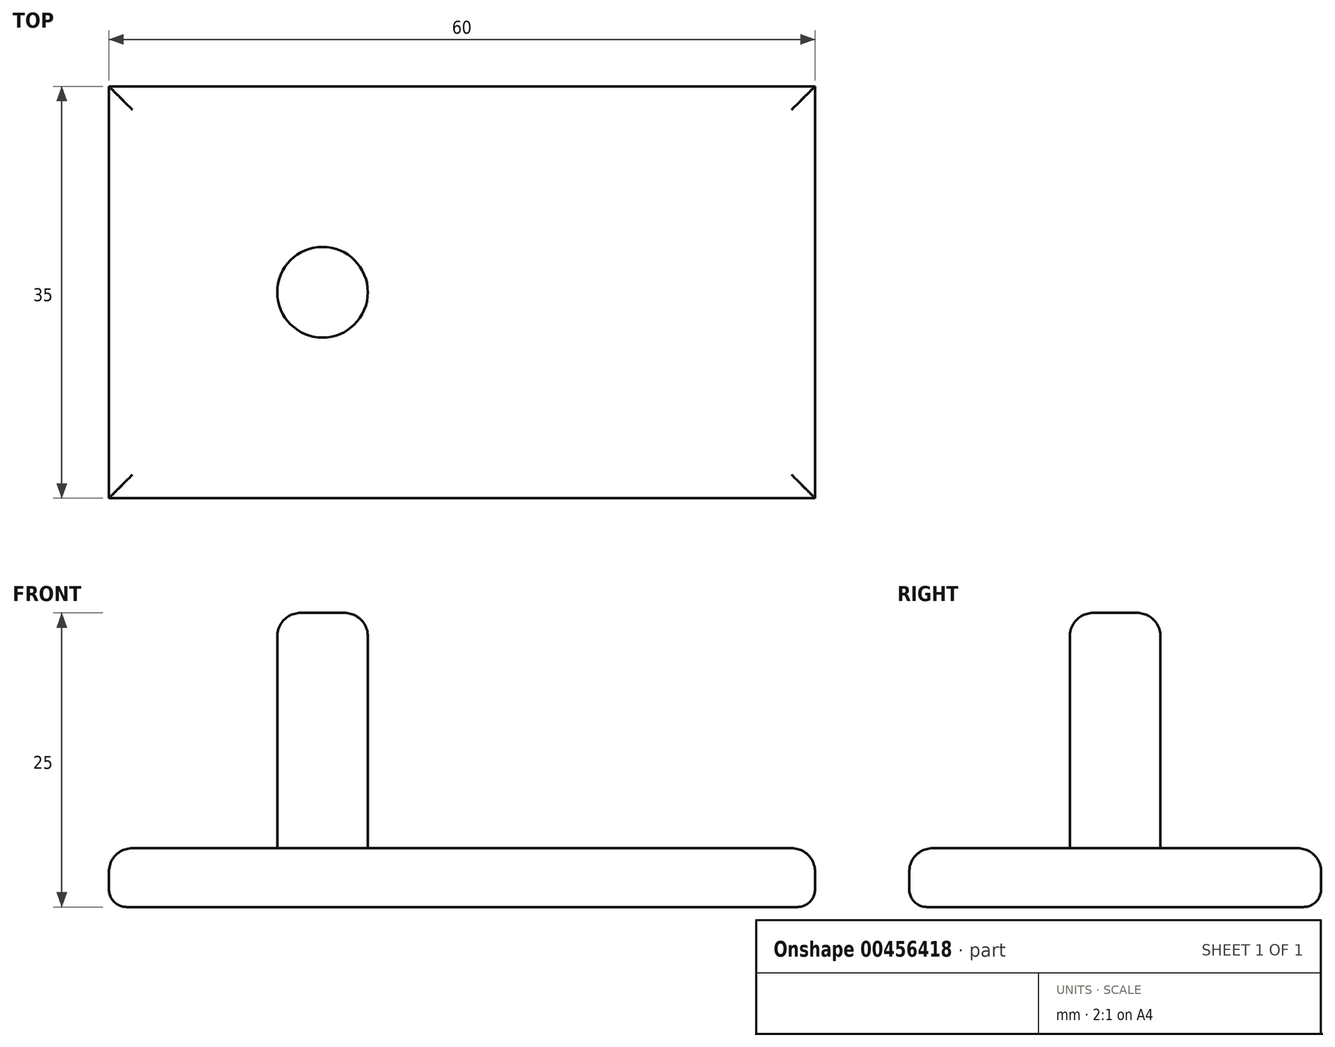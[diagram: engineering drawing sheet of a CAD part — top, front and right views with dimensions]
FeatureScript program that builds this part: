
annotation { "Feature Type Name" : "Feature", "Feature Type Description" : "" }
export const myFeature = defineFeature(function(context is Context, id is Id, definition is map)
    precondition{}
    {
        {
            var Q0;
            Q0=qCreatedBy(makeId("Top.planeOp"),FACE);
            var sketch = newSketch(context, id + "F0", { "sketchPlane" : qUnion([Q0])});
            skLineSegment(sketch, "E0.bottom", {"start": v(-30, 17.5) * mm, "end": v(30, 17.5) * mm});
            skLineSegment(sketch, "E0.top", {"start": v(-30, -17.5) * mm, "end": v(30, -17.5) * mm});
            skLineSegment(sketch, "E0.left", {"start": v(-30, 17.5) * mm, "end": v(-30, -17.5) * mm});
            skLineSegment(sketch, "E0.right", {"start": v(30, 17.5) * mm, "end": v(30, -17.5) * mm});
            skPoint(sketch, "E0.middle", {"position": v(0, 0) * mm});
            skPoint(sketch, "E1.orphan", {"position": v(0, 37.9) * mm});
            skPoint(sketch, "E2.orphan", {"position": v(-61.07, 0) * mm});
            skSolve(sketch);
        }
        {
            var Q0;
            Q0 = qSketchRegion(id + "F0", true);
            extrude(context, id + "F1", {"entities" : qUnion([Q0]), "oppositeDirection" : true, "depth" : 5 * mm});
        }
        {
            var Q0;
            Q0=qCreatedBy(makeId("Top.planeOp"),FACE);
            var sketch = newSketch(context, id + "F2", { "sketchPlane" : qUnion([Q0])});
            skLineSegment(sketch, "E3", {"start": v(-47.54, 0) * mm, "end": v(45.98, 0) * mm, "construction": true});
            skLineSegment(sketch, "E4", {"start": v(45.98, 0) * mm, "end": v(46.2, 1.35) * mm, "construction": true});
            skLineSegment(sketch, "E5", {"start": v(0, 46.27) * mm, "end": v(0, -44.87) * mm, "construction": true});
            skCircle(sketch, "E6", {"center": v(-11.85, 0) * mm, "radius": 3.85 * mm});
            skCircle(sketch, "E7.MirrorC", {"center": v(11.85, 0) * mm, "radius": 3.85 * mm});
            skSolve(sketch);
        }
        {
            var Q0;
            Q0=makeQuery(id+"F2.imprint","IMPRINT",FACE,{"disambiguationData":[TD([[makeQuery(id+"F2.imprint","IMPRINT",EDGE,{"derivedFrom":sQuery(id+"F2.wireOp",EDGE,"E7.MirrorC")}),-1.0]])]});
            var Q1;
            Q1=makeQuery(id+"F2.imprint","IMPRINT",FACE,{"disambiguationData":[TD([[makeQuery(id+"F2.imprint","IMPRINT",EDGE,{"derivedFrom":sQuery(id+"F2.wireOp",EDGE,"E6")}),1.0]])]});
            extrude(context, id + "F3", {"entities" : qUnion([Q0, Q1]), "operationType" : NewBodyOperationType.ADD, "depth" : 20 * mm});
        }
        {
            var Q0;
            Q0=makeQuery(id+"F1.opExtrude","CAP_EDGE",EDGE,{"disambiguationData":[OSD([sQuery(id+"F0.wireOp",EDGE,"E0.top")])],"isStart":true});
            var Q1;
            Q1=makeQuery(id+"F1.opExtrude","CAP_EDGE",EDGE,{"disambiguationData":[OSD([sQuery(id+"F0.wireOp",EDGE,"E0.left")])],"isStart":true});
            var Q2;
            Q2=makeQuery(id+"F1.opExtrude","CAP_EDGE",EDGE,{"disambiguationData":[OSD([sQuery(id+"F0.wireOp",EDGE,"E0.bottom")])],"isStart":true});
            var Q3;
            Q3=makeQuery(id+"F1.opExtrude","CAP_EDGE",EDGE,{"disambiguationData":[OSD([sQuery(id+"F0.wireOp",EDGE,"E0.right")])],"isStart":true});
            var Q4;
            Q4=makeQuery(id+"F3.opExtrude","CAP_EDGE",EDGE,{"disambiguationData":[OSD([sQuery(id+"F2.wireOp",EDGE,"E7.MirrorC")])],"isStart":false});
            var Q5;
            Q5=makeQuery(id+"F3.opExtrude","CAP_EDGE",EDGE,{"disambiguationData":[OSD([sQuery(id+"F2.wireOp",EDGE,"E6")])],"isStart":false});
            fillet(context, id + "F4", {"entities" : qUnion([Q0, Q1, Q2, Q3, Q4, Q5]), "radius" : 2 * mm, "tangentPropagation" : true, "allowEdgeOverflow" : false});
        }
        {
            var Q0;
            Q0=makeQuery(id+"F1.opExtrude","CAP_FACE",FACE,{"disambiguationData":[OSD([sQuery(id+"F0.wireOp",EDGE,"E0.bottom"),sQuery(id+"F0.wireOp",EDGE,"E0.top"),sQuery(id+"F0.wireOp",EDGE,"E0.left"),sQuery(id+"F0.wireOp",EDGE,"E0.right")])],"isStart":false});
            fillet(context, id + "F5", {"entities" : qUnion([Q0]), "radius" : 1.5 * mm, "tangentPropagation" : true, "allowEdgeOverflow" : false});
        }
    });
